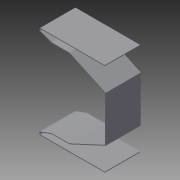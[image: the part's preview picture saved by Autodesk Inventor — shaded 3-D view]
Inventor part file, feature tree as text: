
AUTODESK INVENTOR PART (.ipt)
format: ipt  version: 2015 (Build 190159000, 159)  size: 119,808 bytes
history: native  units: mm
features: other x1, extrude x1, sketch x1
ambient origin geometry x8: Origin, YZ Plane, XZ Plane, XY Plane, X Axis, Y Axis, Z Axis, Center Point
bodies: Body1 (feature_tree)
feature tree (3):
  other  "Sólido1"
  extrude  "Extrusão1"  Depth=40.0mm
  sketch  "Esboço1"  dims[d0=80.0mm d1=20.071286mm d4=20.0mm d5=27.925268mm d6=2.0mm d7=0.904304mm d8=7.71041mm d9=34.664897mm d10=20.674802mm d11=40.0mm d12=0.0mm]
